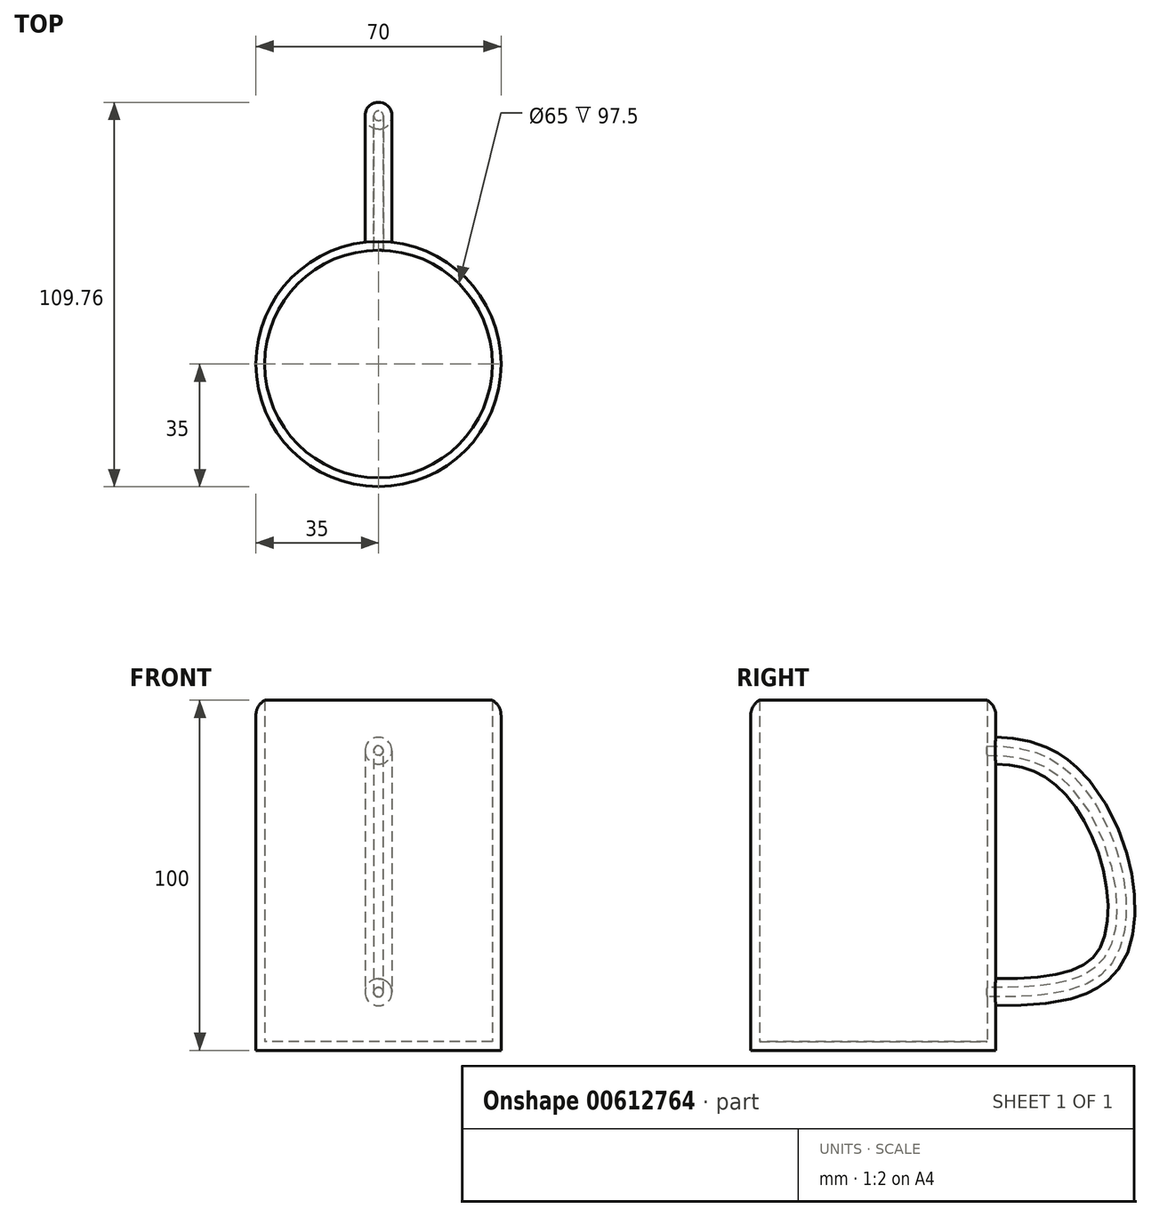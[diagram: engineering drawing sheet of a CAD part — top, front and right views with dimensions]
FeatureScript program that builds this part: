
annotation { "Feature Type Name" : "Feature", "Feature Type Description" : "" }
export const myFeature = defineFeature(function(context is Context, id is Id, definition is map)
    precondition{}
    {
        {
            var Q0;
            Q0=qCreatedBy(makeId("Top.planeOp"),FACE);
            var sketch = newSketch(context, id + "F0", { "sketchPlane" : qUnion([Q0])});
            skCircle(sketch, "E0", {"center": v(0, 0) * mm, "radius": 35 * mm});
            skSolve(sketch);
        }
        {
            var Q0;
            Q0 = qSketchRegion(id + "F0", true);
            extrude(context, id + "F1", {"entities" : qUnion([Q0]), "depth" : 100 * mm, "offsetDistance" : 25 * mm});
        }
        {
            var Q0;
            Q0=qCreatedBy(makeId("Right.planeOp"),FACE);
            var sketch = newSketch(context, id + "F2", { "sketchPlane" : qUnion([Q0])});
            skFitSpline(sketch, "E1", {"points": [v(25.1, 85.23) * mm, v(49.34, 82.23) * mm, v(68.13, 56.48) * mm, v(65.5, 23.96) * mm, v(23.96, 17) * mm], "startDerivative": vector(117.18, 5.4) * mm, "endDerivative": vector(-178.42, 5.6) * mm});
            skSolve(sketch);
        }
        {
            var Q0;
            Q0=qCreatedBy(makeId("Front.planeOp"),FACE);
            cPlane(context, id + "F3", {"entities" : qUnion([Q0]), "cplaneType" : CPlaneType.OFFSET, "offset" : 30 * mm, "oppositeDirection" : true, "width" : 150 * mm, "height" : 150 * mm});
        }
        {
            var Q0;
            Q0=qCreatedBy(id+"F3.planeOp",FACE);
            var sketch = newSketch(context, id + "F4", { "sketchPlane" : qUnion([Q0])});
            skCircle(sketch, "E2", {"center": v(0, 85.57) * mm, "radius": 3.85 * mm});
            skSolve(sketch);
        }
        {
            var Q0;
            Q0 = qSketchRegion(id + "F4", true);
            var Q1;
            Q1=sQuery(id+"F2.wireOp",EDGE,"E1");
            sweep(context, id + "F5", {"operationType" : NewBodyOperationType.ADD, "profiles" : qUnion([Q0]), "path" : qUnion([Q1])});
        }
        {
            var Q0;
            Q0=makeQuery(id+"F1.opExtrude","CAP_FACE",FACE,{"disambiguationData":[OSD([sQuery(id+"F0.wireOp",EDGE,"E0")])],"isStart":false});
            shell(context, id + "F6", {"entities" : qUnion([Q0]), "thickness" : 2.5 * mm});
        }
        {
            var Q0;
            Q0=makeQuery(id+"F1.opExtrude","CAP_EDGE",EDGE,{"disambiguationData":[OSD([sQuery(id+"F0.wireOp",EDGE,"E0")])],"isStart":false});
            fillet(context, id + "F7", {"entities" : qUnion([Q0]), "radius" : 5 * mm, "tangentPropagation" : true, "allowEdgeOverflow" : false});
        }
    });
